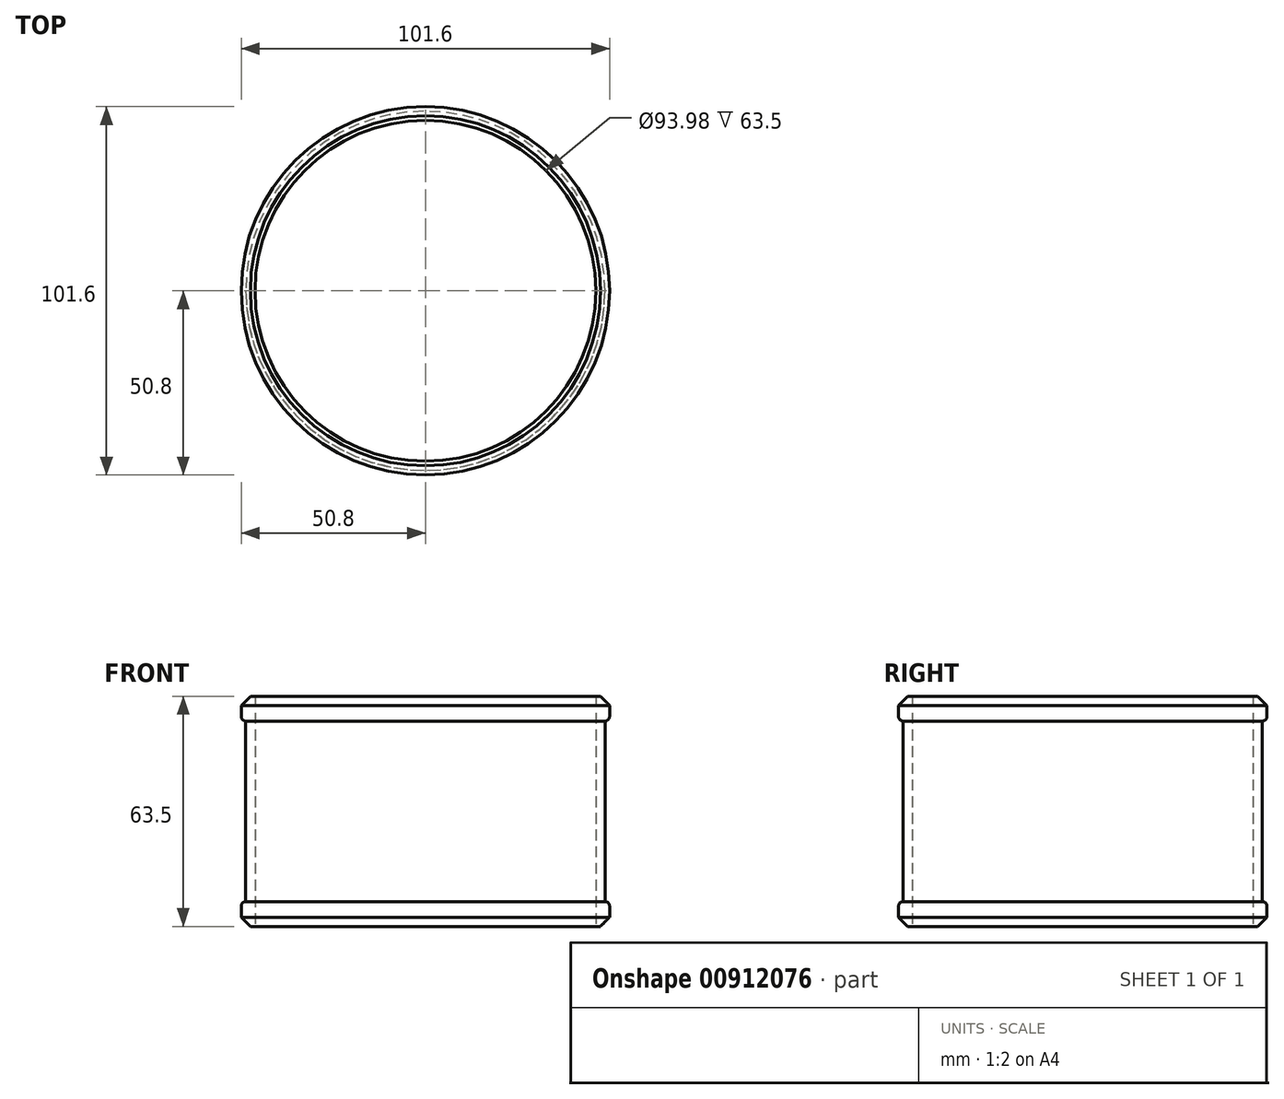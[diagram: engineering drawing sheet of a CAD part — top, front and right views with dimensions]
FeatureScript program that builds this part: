
annotation { "Feature Type Name" : "Feature", "Feature Type Description" : "" }
export const myFeature = defineFeature(function(context is Context, id is Id, definition is map)
    precondition{}
    {
        {
            var Q0;
            Q0=qCreatedBy(makeId("Top.planeOp"),FACE);
            var sketch = newSketch(context, id + "F0", { "sketchPlane" : qUnion([Q0])});
            skCircle(sketch, "E0", {"center": v(0, 0) * mm, "radius": 49.53 * mm});
            skCircle(sketch, "E1", {"center": v(0, 0) * mm, "radius": 47 * mm});
            skSolve(sketch);
        }
        {
            var Q0;
            Q0=makeQuery(id+"F0.imprint","IMPRINT",FACE,{"disambiguationData":[TD([[makeQuery(id+"F0.imprint","IMPRINT",EDGE,{"derivedFrom":sQuery(id+"F0.wireOp",EDGE,"E0")}),1.0]])]});
            extrude(context, id + "F1", {"entities" : qUnion([Q0]), "depth" : 63.5 * mm, "offsetDistance" : 25.4 * mm});
        }
        {
            var Q0;
            Q0=makeQuery(id+"F1.opExtrude","CAP_FACE",FACE,{"disambiguationData":[OSD([sQuery(id+"F0.wireOp",EDGE,"E0"),sQuery(id+"F0.wireOp",EDGE,"E1")])],"isStart":false});
            var sketch = newSketch(context, id + "F2", { "sketchPlane" : qUnion([Q0])});
            skCircle(sketch, "E2", {"center": v(0, 0) * mm, "radius": 50.8 * mm});
            skSolve(sketch);
        }
        {
            var Q0;
            Q0=makeQuery(id+"F2.imprint","IMPRINT",FACE,{"disambiguationData":[TD([[makeQuery(id+"F2.imprint","IMPRINT",EDGE,{"derivedFrom":sQuery(id+"F2.wireOp",EDGE,"E2")}),1.0]])]});
            extrude(context, id + "F3", {"entities" : qUnion([Q0]), "operationType" : NewBodyOperationType.ADD, "oppositeDirection" : true, "depth" : 6.86 * mm, "offsetDistance" : 25.4 * mm});
        }
        {
            var Q0;
            Q0=makeQuery(id+"F3.opExtrude","CAP_EDGE",EDGE,{"disambiguationData":[OSD([sQuery(id+"F2.wireOp",EDGE,"E2")])],"isStart":true});
            chamfer(context, id + "F4", {"entities" : qUnion([Q0]), "width" : 2.54 * mm, "tangentPropagation" : true});
        }
        {
            var Q0;
            Q0=makeQuery(id+"F3.opExtrude","CAP_EDGE",EDGE,{"disambiguationData":[OSD([sQuery(id+"F2.wireOp",EDGE,"E2")])],"isStart":false});
            fillet(context, id + "F5", {"entities" : qUnion([Q0]), "radius" : 1.27 * mm, "tangentPropagation" : true, "allowEdgeOverflow" : false});
        }
        {
            var Q0;
            Q0=makeQuery(id+"F1.opExtrude","CAP_FACE",FACE,{"disambiguationData":[OSD([sQuery(id+"F0.wireOp",EDGE,"E0"),sQuery(id+"F0.wireOp",EDGE,"E1")])],"isStart":true});
            var sketch = newSketch(context, id + "F6", { "sketchPlane" : qUnion([Q0])});
            skCircle(sketch, "E3", {"center": v(0, 0) * mm, "radius": 50.8 * mm});
            skSolve(sketch);
        }
        {
            var Q0;
            Q0=makeQuery(id+"F6.imprint","IMPRINT",FACE,{"disambiguationData":[TD([[makeQuery(id+"F6.imprint","IMPRINT",EDGE,{"derivedFrom":sQuery(id+"F6.wireOp",EDGE,"E3")}),1.0]])]});
            extrude(context, id + "F7", {"entities" : qUnion([Q0]), "operationType" : NewBodyOperationType.ADD, "oppositeDirection" : true, "depth" : 6.86 * mm, "offsetDistance" : 25.4 * mm});
        }
        {
            var Q0;
            Q0=makeQuery(id+"F7.opExtrude","CAP_EDGE",EDGE,{"disambiguationData":[OSD([sQuery(id+"F6.wireOp",EDGE,"E3")])],"isStart":true});
            chamfer(context, id + "F8", {"entities" : qUnion([Q0]), "width" : 2.54 * mm, "tangentPropagation" : true});
        }
        {
            var Q0;
            Q0=makeQuery(id+"F7.opExtrude","CAP_EDGE",EDGE,{"disambiguationData":[OSD([sQuery(id+"F6.wireOp",EDGE,"E3")])],"isStart":false});
            fillet(context, id + "F9", {"entities" : qUnion([Q0]), "radius" : 1.27 * mm, "tangentPropagation" : true, "allowEdgeOverflow" : false});
        }
    });
